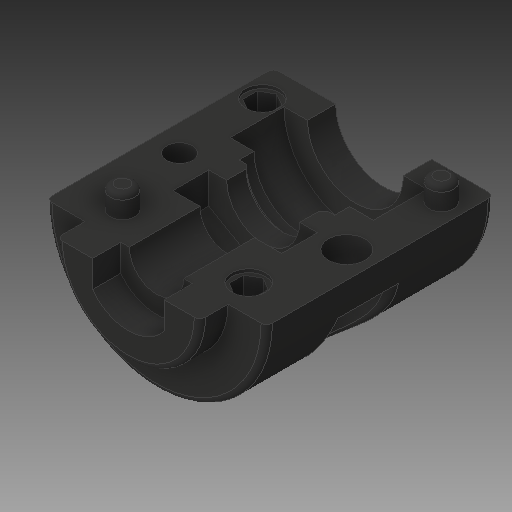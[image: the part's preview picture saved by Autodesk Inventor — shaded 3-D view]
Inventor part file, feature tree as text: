
AUTODESK INVENTOR PART (.ipt)
format: ipt  version: 2018 (Build 220112000, 112)  size: 286,720 bytes
history: native  units: in
note: dims shown in document units (in); Inventor stores cm internally (conversion verified against a paired STEP export)
features: fillet x1
ambient origin geometry x8: Origin, YZ Plane, XZ Plane, XY Plane, X Axis, Y Axis, Z Axis, Center Point
bodies: Solid1 (feature_tree)
feature tree (1):
  fillet  "Fillet1"  [1 undecoded]
note: 1 required parameter value undecoded (feature->parameter linkage not recoverable at this tier; creation-order binding heuristic only, values carry confidence <= 0.55)
